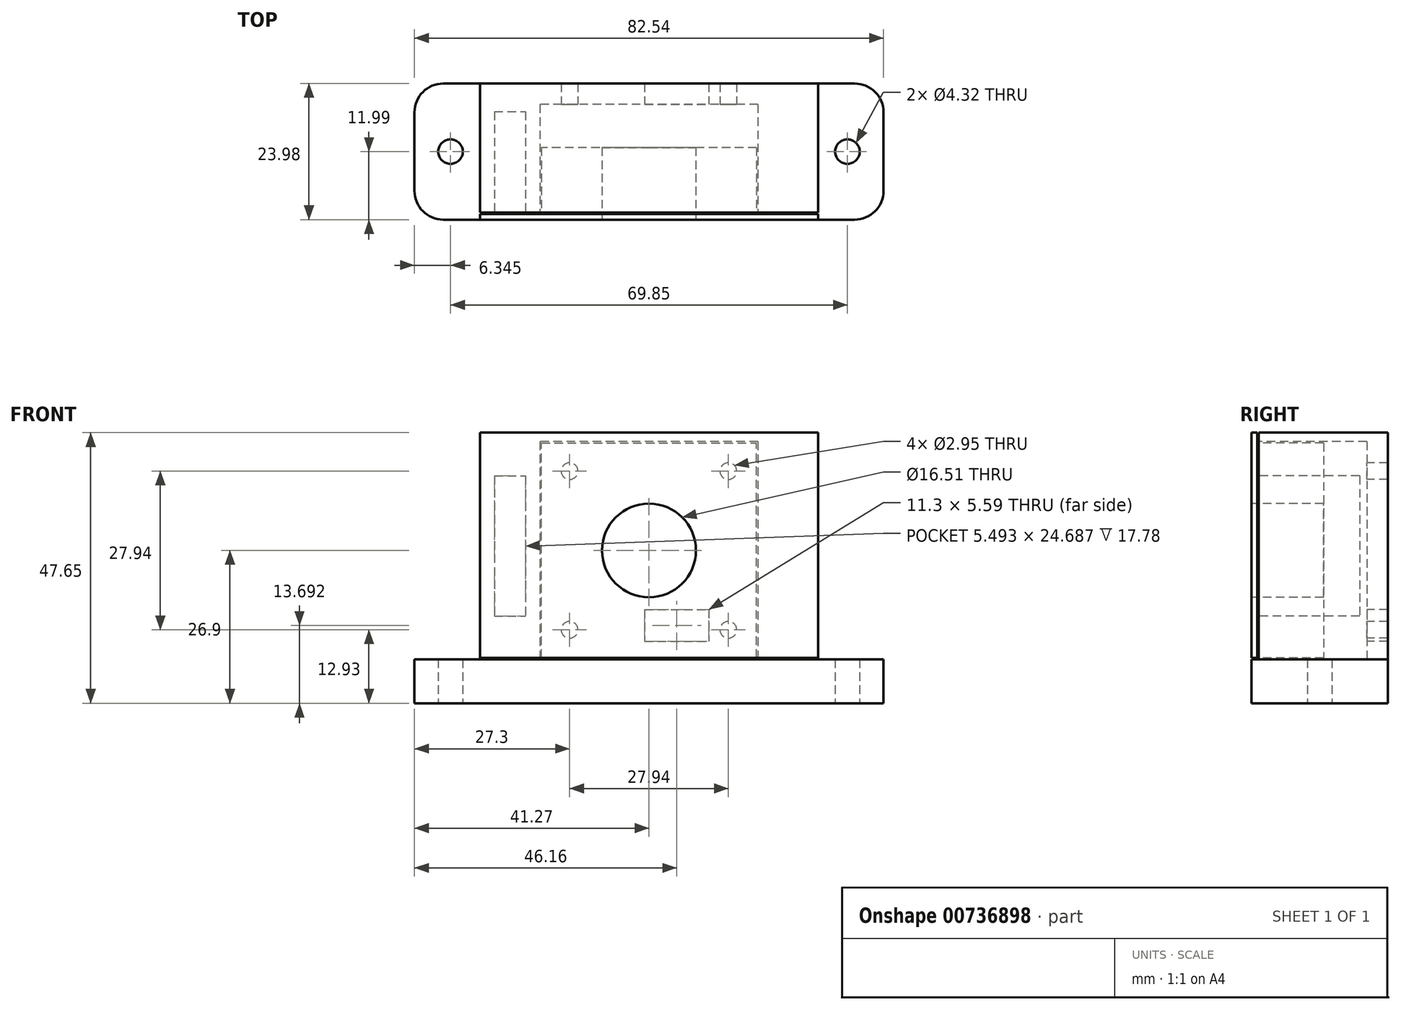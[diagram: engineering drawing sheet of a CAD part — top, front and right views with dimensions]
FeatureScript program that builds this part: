
annotation { "Feature Type Name" : "Feature", "Feature Type Description" : "" }
export const myFeature = defineFeature(function(context is Context, id is Id, definition is map)
    precondition{}
    {
        {
            var Q0;
            Q0=qCreatedBy(makeId("Front.planeOp"),FACE);
            var sketch = newSketch(context, id + "F0", { "sketchPlane" : qUnion([Q0])});
            skLineSegment(sketch, "E0.bottom", {"start": v(-29.75, 20.75) * mm, "end": v(29.75, 20.75) * mm});
            skLineSegment(sketch, "E0.top", {"start": v(-29.75, -20.75) * mm, "end": v(29.75, -20.75) * mm});
            skLineSegment(sketch, "E0.left", {"start": v(-29.75, 20.75) * mm, "end": v(-29.75, -20.75) * mm});
            skLineSegment(sketch, "E0.right", {"start": v(29.75, 20.75) * mm, "end": v(29.75, -20.75) * mm});
            skPoint(sketch, "E0.middle", {"position": v(0, 0) * mm});
            skCircle(sketch, "E1", {"center": v(14.45, 7.05) * mm, "radius": 11.5 * mm});
            skCircle(sketch, "E2", {"center": v(-17.25, -10.75) * mm, "radius": 6 * mm});
            skLineSegment(sketch, "E3.bottom", {"start": v(-22.75, 15.75) * mm, "end": v(-11.25, 15.75) * mm});
            skLineSegment(sketch, "E3.top", {"start": v(-22.75, -1.25) * mm, "end": v(-11.25, -1.25) * mm});
            skLineSegment(sketch, "E3.left", {"start": v(-23.75, 14.75) * mm, "end": v(-23.75, -0.25) * mm});
            skLineSegment(sketch, "E3.right", {"start": v(-10.25, 14.75) * mm, "end": v(-10.25, -0.25) * mm});
            skPoint(sketch, "E4.visualSharp", {"position": v(-10.25, 15.75) * mm});
            skArc(sketch, "E4.filletArc", {"start": v(-10.25, 14.75) * mm, "mid": v(-10.54, 15.46) * mm, "end": v(-11.25, 15.75) * mm});
            skPoint(sketch, "E5.visualSharp", {"position": v(-10.25, -1.25) * mm});
            skArc(sketch, "E5.filletArc", {"start": v(-11.25, -1.25) * mm, "mid": v(-10.54, -0.96) * mm, "end": v(-10.25, -0.25) * mm});
            skPoint(sketch, "E6.visualSharp", {"position": v(-23.75, -1.25) * mm});
            skArc(sketch, "E6.filletArc", {"start": v(-23.75, -0.25) * mm, "mid": v(-23.46, -0.96) * mm, "end": v(-22.75, -1.25) * mm});
            skPoint(sketch, "E7.visualSharp", {"position": v(-23.75, 15.75) * mm});
            skArc(sketch, "E7.filletArc", {"start": v(-22.75, 15.75) * mm, "mid": v(-23.46, 15.46) * mm, "end": v(-23.75, 14.75) * mm});
            skSolve(sketch);
        }
        {
            var Q0;
            Q0=qSketchRegion(id+"F0",true);
            var Q1;
            Q1=makeQuery(id+"F0.imprint","IMPRINT",FACE,{"disambiguationData":[TD([[makeQuery(id+"F0.imprint","IMPRINT",EDGE,{"derivedFrom":sQuery(id+"F0.wireOp",EDGE,"E3.bottom")}),-1.0]])]});
            var Q2;
            Q2=makeQuery(id+"F0.imprint","IMPRINT",FACE,{"disambiguationData":[TD([[makeQuery(id+"F0.imprint","IMPRINT",EDGE,{"derivedFrom":sQuery(id+"F0.wireOp",EDGE,"E1")}),1.0]])]});
            var Q3;
            Q3=makeQuery(id+"F0.imprint","IMPRINT",FACE,{"disambiguationData":[TD([[makeQuery(id+"F0.imprint","IMPRINT",EDGE,{"derivedFrom":sQuery(id+"F0.wireOp",EDGE,"E2")}),1.0]])]});
            extrude(context, id + "F1", {"entities" : qUnion([Q0, Q1, Q2, Q3]), "oppositeDirection" : true, "depth" : 21.5 * mm, "offsetDistance" : 25 * mm});
        }
        {
            var Q0;
            Q0=makeQuery(id+"F1.opExtrude","SWEPT_FACE",FACE,{"disambiguationData":[OSD([sQuery(id+"F0.wireOp",EDGE,"E0.left")])]});
            var sketch = newSketch(context, id + "F2", { "sketchPlane" : qUnion([Q0])});
            skCircle(sketch, "E8", {"center": v(-10, -11.25) * mm, "radius": 2.5 * mm});
            skSolve(sketch);
        }
        {
            var Q0;
            Q0=makeQuery(id+"F1.opExtrude","SWEPT_FACE",FACE,{"disambiguationData":[OSD([sQuery(id+"F0.wireOp",EDGE,"E0.bottom")])]});
            var sketch = newSketch(context, id + "F3", { "sketchPlane" : qUnion([Q0])});
            skCircle(sketch, "E9", {"center": v(-17.25, 10.5) * mm, "radius": 6 * mm});
            skSolve(sketch);
        }
        {
            var Q0;
            Q0=makeQuery(id+"F1.opExtrude","SWEPT_FACE",FACE,{"disambiguationData":[OSD([sQuery(id+"F0.wireOp",EDGE,"E0.right")])]});
            var sketch = newSketch(context, id + "F4", { "sketchPlane" : qUnion([Q0])});
            skLineSegment(sketch, "E10.bottom", {"start": v(5.5, 6.25) * mm, "end": v(15.5, 6.25) * mm});
            skLineSegment(sketch, "E10.top", {"start": v(5.5, -14.25) * mm, "end": v(15.5, -14.25) * mm});
            skLineSegment(sketch, "E10.left", {"start": v(3.5, 4.25) * mm, "end": v(3.5, -12.25) * mm});
            skLineSegment(sketch, "E10.right", {"start": v(17.5, 4.25) * mm, "end": v(17.5, -12.25) * mm});
            skPoint(sketch, "E11.visualSharp", {"position": v(3.5, 6.25) * mm});
            skArc(sketch, "E11.filletArc", {"start": v(5.5, 6.25) * mm, "mid": v(4.09, 5.66) * mm, "end": v(3.5, 4.25) * mm});
            skPoint(sketch, "E12.visualSharp", {"position": v(17.5, 6.25) * mm});
            skArc(sketch, "E12.filletArc", {"start": v(17.5, 4.25) * mm, "mid": v(16.91, 5.66) * mm, "end": v(15.5, 6.25) * mm});
            skPoint(sketch, "E13.visualSharp", {"position": v(17.5, -14.25) * mm});
            skArc(sketch, "E13.filletArc", {"start": v(15.5, -14.25) * mm, "mid": v(16.91, -13.66) * mm, "end": v(17.5, -12.25) * mm});
            skPoint(sketch, "E14.visualSharp", {"position": v(3.5, -14.25) * mm});
            skArc(sketch, "E14.filletArc", {"start": v(3.5, -12.25) * mm, "mid": v(4.09, -13.66) * mm, "end": v(5.5, -14.25) * mm});
            skSolve(sketch);
        }
        {
            var Q0;
            Q0=makeQuery(id+"F0.imprint","IMPRINT",FACE,{"disambiguationData":[TD([[makeQuery(id+"F0.imprint","IMPRINT",EDGE,{"derivedFrom":sQuery(id+"F0.wireOp",EDGE,"E0.bottom")}),-1.0]])]});
            var sketch = newSketch(context, id + "F5", { "sketchPlane" : qUnion([Q0])});
            skLineSegment(sketch, "E15.bottom", {"start": v(-29.75, 20.75) * mm, "end": v(29.75, 20.75) * mm});
            skLineSegment(sketch, "E15.top", {"start": v(-29.75, -20.75) * mm, "end": v(29.75, -20.75) * mm});
            skLineSegment(sketch, "E15.left", {"start": v(-29.75, 20.75) * mm, "end": v(-29.75, -20.75) * mm});
            skLineSegment(sketch, "E15.right", {"start": v(29.75, 20.75) * mm, "end": v(29.75, -20.75) * mm});
            skSolve(sketch);
        }
        {
            var Q0;
            Q0 = qSketchRegion(id + "F5", true);
            extrude(context, id + "F6", {"entities" : qUnion([Q0]), "operationType" : NewBodyOperationType.REMOVE, "endBound" : BoundingType.THROUGH_ALL, "depth" : 25 * mm, "offsetDistance" : 25 * mm});
        }
        {
            var Q0;
            Q0=makeQuery(id+"F6.boolean.opBoolean","MERGE",FACE,{"derivedFrom":[makeQuery(id+"F1.opExtrude","CAP_FACE",FACE,{"disambiguationData":[OSD([sQuery(id+"F0.wireOp",EDGE,"E0.bottom"),sQuery(id+"F0.wireOp",EDGE,"E0.top"),sQuery(id+"F0.wireOp",EDGE,"E0.left"),sQuery(id+"F0.wireOp",EDGE,"E0.right")])],"isStart":true}),makeQuery(id+"F6.opExtrude","CAP_FACE",FACE,{"disambiguationData":[OSD([sQuery(id+"F5.wireOp",EDGE,"E15.bottom"),sQuery(id+"F5.wireOp",EDGE,"E15.top"),sQuery(id+"F5.wireOp",EDGE,"E15.left"),sQuery(id+"F5.wireOp",EDGE,"E15.right")])],"isStart":true})]});
            var sketch = newSketch(context, id + "F7", { "sketchPlane" : qUnion([Q0])});
            skLineSegment(sketch, "E16.bottom", {"start": v(19.18, 19.18) * mm, "end": v(-19.18, 19.18) * mm});
            skLineSegment(sketch, "E16.top", {"start": v(19.18, -19.18) * mm, "end": v(-19.18, -19.18) * mm});
            skLineSegment(sketch, "E16.left", {"start": v(19.18, 19.18) * mm, "end": v(19.18, -19.18) * mm});
            skLineSegment(sketch, "E16.right", {"start": v(-19.18, 19.18) * mm, "end": v(-19.18, -19.18) * mm});
            skPoint(sketch, "E16.middle", {"position": v(0, 0) * mm});
            skSolve(sketch);
        }
        {
            var Q0;
            Q0 = qSketchRegion(id + "F7", true);
            extrude(context, id + "F8", {"entities" : qUnion([Q0]), "operationType" : NewBodyOperationType.REMOVE, "oppositeDirection" : true, "depth" : 19.05 * mm, "offsetDistance" : 25 * mm});
        }
        {
            var Q0;
            Q0=makeQuery(id+"F8.boolean.opBoolean","COPY",FACE,{"derivedFrom":makeQuery(id+"F8.opExtrude","CAP_FACE",FACE,{"disambiguationData":[OSD([sQuery(id+"F7.wireOp",EDGE,"E16.bottom"),sQuery(id+"F7.wireOp",EDGE,"E16.top"),sQuery(id+"F7.wireOp",EDGE,"E16.left"),sQuery(id+"F7.wireOp",EDGE,"E16.right")])],"isStart":false})});
            var sketch = newSketch(context, id + "F9", { "sketchPlane" : qUnion([Q0])});
            skLineSegment(sketch, "E17.bottom", {"start": v(-0.76, -10.41) * mm, "end": v(10.54, -10.41) * mm});
            skLineSegment(sketch, "E17.top", {"start": v(-0.76, -16) * mm, "end": v(10.54, -16) * mm});
            skLineSegment(sketch, "E17.left", {"start": v(-0.76, -10.41) * mm, "end": v(-0.76, -16) * mm});
            skLineSegment(sketch, "E17.right", {"start": v(10.54, -10.41) * mm, "end": v(10.54, -16) * mm});
            skSolve(sketch);
        }
        {
            var Q0;
            Q0=makeQuery(id+"F9.imprint","IMPRINT",FACE,{"disambiguationData":[TD([[makeQuery(id+"F9.imprint","IMPRINT",EDGE,{"derivedFrom":sQuery(id+"F9.wireOp",EDGE,"E17.bottom")}),-1.0]])]});
            extrude(context, id + "F10", {"entities" : qUnion([Q0]), "operationType" : NewBodyOperationType.REMOVE, "endBound" : BoundingType.THROUGH_ALL, "oppositeDirection" : true, "depth" : 25.4 * mm, "offsetDistance" : 25.4 * mm});
        }
        {
            var Q0;
            Q0=makeQuery(id+"F8.boolean.opBoolean","COPY",FACE,{"derivedFrom":makeQuery(id+"F8.opExtrude","CAP_FACE",FACE,{"disambiguationData":[OSD([sQuery(id+"F7.wireOp",EDGE,"E16.bottom"),sQuery(id+"F7.wireOp",EDGE,"E16.top"),sQuery(id+"F7.wireOp",EDGE,"E16.left"),sQuery(id+"F7.wireOp",EDGE,"E16.right")])],"isStart":false})});
            var sketch = newSketch(context, id + "F11", { "sketchPlane" : qUnion([Q0])});
            skLineSegment(sketch, "E18.bottom", {"start": v(13.97, 13.97) * mm, "end": v(-13.97, 13.97) * mm, "construction": true});
            skLineSegment(sketch, "E18.top", {"start": v(13.97, -13.97) * mm, "end": v(-13.97, -13.97) * mm, "construction": true});
            skLineSegment(sketch, "E18.left", {"start": v(13.97, 13.97) * mm, "end": v(13.97, -13.97) * mm, "construction": true});
            skLineSegment(sketch, "E18.right", {"start": v(-13.97, 13.97) * mm, "end": v(-13.97, -13.97) * mm, "construction": true});
            skPoint(sketch, "E18.middle", {"position": v(0, 0) * mm});
            skSolve(sketch);
        }
        {
            var Q0;
            Q0=sQuery(id+"F11.wireOp",VERTEX,"E18.bottom.end");
            var Q1;
            Q1=sQuery(id+"F11.wireOp",VERTEX,"E18.bottom.start");
            var Q2;
            Q2=sQuery(id+"F11.wireOp",VERTEX,"E18.left.end");
            var Q3;
            Q3=sQuery(id+"F11.wireOp",VERTEX,"E18.right.end");
            var Q4;
            Q4=makeQuery(id+"F1.opExtrude","SWEPT_BODY",BODY,{"disambiguationData":[OSD([sQuery(id+"F0.wireOp",EDGE,"E0.bottom"),sQuery(id+"F0.wireOp",EDGE,"E0.top"),sQuery(id+"F0.wireOp",EDGE,"E0.left"),sQuery(id+"F0.wireOp",EDGE,"E0.right")])]});
            hole(context, id + "F12", {"style" : HoleStyle.SIMPLE, "endStyle" : HoleEndStyle.THROUGH, "standardTappedOrClearance" : lookupTablePath({ "standard" : "ANSI", "fit" : "Close", "size" : "#4", "type" : "Clearance" }), "standardBlindInLast" : lookupTablePath({ "fit" : "Close", "standard" : "ANSI", "size" : "#4", "type" : "Clearance" }), "holeDiameter" : 2.95 * mm, "majorDiameter" : 6.35 * mm, "isTappedThrough" : true, "tappedDepth" : 12.7 * mm, "tapClearance" : 3, "locations" : qUnion([Q0, Q1, Q2, Q3]), "scope" : qUnion([Q4])});
        }
        {
            var Q0;
            Q0=makeQuery(id+"F4.imprint","IMPRINT",FACE,{"disambiguationData":[TD([[makeQuery(id+"F4.imprint","IMPRINT",EDGE,{"derivedFrom":sQuery(id+"F4.wireOp",EDGE,"E10.bottom")}),1.0]])]});
            var sketch = newSketch(context, id + "F13", { "sketchPlane" : qUnion([Q0])});
            skLineSegment(sketch, "E19.bottom", {"start": v(0.34, -20.75) * mm, "end": v(21.16, -20.75) * mm});
            skLineSegment(sketch, "E19.top", {"start": v(0.34, -25.32) * mm, "end": v(21.16, -25.32) * mm});
            skLineSegment(sketch, "E19.right", {"start": v(21.16, -20.75) * mm, "end": v(21.16, -25.32) * mm});
            skLineSegment(sketch, "E20", {"start": v(0.34, -20.75) * mm, "end": v(0.34, -25.32) * mm});
            skLineSegment(sketch, "E21.bottom", {"start": v(-1.24, -19.18) * mm, "end": v(22.74, -19.18) * mm});
            skLineSegment(sketch, "E21.top", {"start": v(-1.24, -26.9) * mm, "end": v(22.74, -26.9) * mm});
            skLineSegment(sketch, "E21.left", {"start": v(-1.24, -19.18) * mm, "end": v(-1.24, -26.9) * mm});
            skLineSegment(sketch, "E21.right", {"start": v(22.74, -19.18) * mm, "end": v(22.74, -26.9) * mm});
            skLineSegment(sketch, "E22", {"start": v(10.75, -20.75) * mm, "end": v(10.75, -19.18) * mm, "construction": true});
            skLineSegment(sketch, "E23", {"start": v(22.74, -23.04) * mm, "end": v(21.16, -23.04) * mm, "construction": true});
            skLineSegment(sketch, "E24", {"start": v(10.75, -25.32) * mm, "end": v(10.75, -26.9) * mm, "construction": true});
            skLineSegment(sketch, "E25", {"start": v(0.34, -23.04) * mm, "end": v(-1.24, -23.04) * mm, "construction": true});
            skSolve(sketch);
        }
        {
            var Q0;
            Q0 = qSketchRegion(id + "F13", true);
            var Q1;
            Q1=makeQuery(id+"F1.opExtrude","SWEPT_FACE",FACE,{"disambiguationData":[OSD([sQuery(id+"F0.wireOp",EDGE,"E0.left")])]});
            extrude(context, id + "F14", {"entities" : qUnion([Q0]), "operationType" : NewBodyOperationType.ADD, "endBound" : BoundingType.UP_TO_SURFACE, "oppositeDirection" : true, "depth" : 25.4 * mm, "endBoundEntityFace" : qUnion([Q1]), "offsetDistance" : 25.4 * mm});
        }
        {
            var Q0;
            Q0=makeQuery(id+"F1.opExtrude","CAP_FACE",FACE,{"disambiguationData":[OSD([sQuery(id+"F0.wireOp",EDGE,"E0.bottom"),sQuery(id+"F0.wireOp",EDGE,"E0.top"),sQuery(id+"F0.wireOp",EDGE,"E0.left"),sQuery(id+"F0.wireOp",EDGE,"E0.right")])],"isStart":false});
            var Q1;
            Q1=makeQuery(id+"F14.opExtrude","SWEPT_FACE",FACE,{"disambiguationData":[OSD([sQuery(id+"F13.wireOp",EDGE,"E21.right")])]});
            extrude(context, id + "F15", {"entities" : qUnion([Q0]), "operationType" : NewBodyOperationType.ADD, "endBound" : BoundingType.UP_TO_SURFACE, "depth" : 25.4 * mm, "endBoundEntityFace" : qUnion([Q1]), "offsetDistance" : 25.4 * mm});
        }
        {
            var Q0;
            Q0=makeQuery(id+"F1.opExtrude","CAP_FACE",FACE,{"disambiguationData":[OSD([sQuery(id+"F0.wireOp",EDGE,"E0.bottom"),sQuery(id+"F0.wireOp",EDGE,"E0.top"),sQuery(id+"F0.wireOp",EDGE,"E0.left"),sQuery(id+"F0.wireOp",EDGE,"E0.right")])],"isStart":true});
            var sketch = newSketch(context, id + "F16", { "sketchPlane" : qUnion([Q0])});
            skLineSegment(sketch, "E26.bottom", {"start": v(-27.21, 13.13) * mm, "end": v(-21.72, 13.13) * mm});
            skLineSegment(sketch, "E26.top", {"start": v(-27.21, -11.56) * mm, "end": v(-21.72, -11.56) * mm});
            skLineSegment(sketch, "E26.left", {"start": v(-27.2, 13.13) * mm, "end": v(-27.21, -11.56) * mm});
            skLineSegment(sketch, "E26.right", {"start": v(-21.72, 13.13) * mm, "end": v(-21.72, -11.56) * mm});
            skSolve(sketch);
        }
        {
            var Q0;
            Q0 = qSketchRegion(id + "F16", true);
            extrude(context, id + "F17", {"entities" : qUnion([Q0]), "operationType" : NewBodyOperationType.REMOVE, "oppositeDirection" : true, "depth" : 17.78 * mm, "offsetDistance" : 25.4 * mm});
        }
        {
            var Q0;
            Q0=makeQuery(id+"F14.opExtrude","SWEPT_FACE",FACE,{"disambiguationData":[OSD([sQuery(id+"F13.wireOp",EDGE,"E21.left")])]});
            var sketch = newSketch(context, id + "F18", { "sketchPlane" : qUnion([Q0])});
            skLineSegment(sketch, "E27.2", {"start": v(-18.92, -18.92) * mm, "end": v(18.92, -18.92) * mm});
            skCircle(sketch, "E28", {"center": v(0, 0) * mm, "radius": 8.26 * mm});
            skLineSegment(sketch, "E29.0", {"start": v(-18.92, 18.92) * mm, "end": v(-18.92, -18.92) * mm});
            skLineSegment(sketch, "E29.1", {"start": v(18.92, 18.92) * mm, "end": v(-18.92, 18.92) * mm});
            skLineSegment(sketch, "E29.2", {"start": v(18.92, 18.92) * mm, "end": v(18.92, -18.92) * mm});
            skSolve(sketch);
        }
        {
            var Q0;
            Q0 = qSketchRegion(id + "F18", true);
            extrude(context, id + "F19", {"entities" : qUnion([Q0]), "oppositeDirection" : true, "depth" : 12.7 * mm, "offsetDistance" : 25.4 * mm});
        }
        {
            var Q0;
            Q0=makeQuery(id+"F19.opExtrude","CAP_FACE",FACE,{"disambiguationData":[OSD([sQuery(id+"F18.wireOp",EDGE,"E27.2"),sQuery(id+"F18.wireOp",EDGE,"E28"),sQuery(id+"F18.wireOp",EDGE,"E29.0"),sQuery(id+"F18.wireOp",EDGE,"E29.1"),sQuery(id+"F18.wireOp",EDGE,"E29.2")])],"isStart":true});
            var sketch = newSketch(context, id + "F20", { "sketchPlane" : qUnion([Q0])});
            skLineSegment(sketch, "E30.bottom", {"start": v(-29.75, 20.75) * mm, "end": v(29.75, 20.75) * mm});
            skLineSegment(sketch, "E30.top", {"start": v(-29.75, -18.92) * mm, "end": v(29.75, -18.92) * mm});
            skLineSegment(sketch, "E30.left", {"start": v(-29.75, 20.75) * mm, "end": v(-29.75, -18.92) * mm});
            skLineSegment(sketch, "E30.right", {"start": v(29.75, 20.75) * mm, "end": v(29.75, -18.92) * mm});
            skCircle(sketch, "E31.0", {"center": v(0, 0) * mm, "radius": 8.26 * mm});
            skSolve(sketch);
        }
        {
            var Q0;
            Q0 = qSketchRegion(id + "F20", true);
            extrude(context, id + "F21", {"entities" : qUnion([Q0]), "operationType" : NewBodyOperationType.ADD, "oppositeDirection" : true, "depth" : 1.02 * mm, "offsetDistance" : 25.4 * mm});
        }
        {
            var Q0;
            Q0=qCreatedBy(makeId("Right.planeOp"),FACE);
            var sketch = newSketch(context, id + "F22", { "sketchPlane" : qUnion([Q0])});
            skLineSegment(sketch, "E32.bottom", {"start": v(22.74, -19.18) * mm, "end": v(-1.24, -19.18) * mm});
            skLineSegment(sketch, "E32.top", {"start": v(22.74, -26.9) * mm, "end": v(-1.24, -26.9) * mm});
            skLineSegment(sketch, "E32.left", {"start": v(22.74, -19.18) * mm, "end": v(22.74, -26.9) * mm});
            skLineSegment(sketch, "E32.right", {"start": v(-1.24, -19.18) * mm, "end": v(-1.24, -26.9) * mm});
            skSolve(sketch);
        }
        {
            var Q0;
            Q0 = qSketchRegion(id + "F22", true);
            extrude(context, id + "F23", {"entities" : qUnion([Q0]), "operationType" : NewBodyOperationType.ADD, "endBound" : BoundingType.SYMMETRIC, "depth" : 82.55 * mm, "offsetDistance" : 25.4 * mm});
        }
        {
            var Q0;
            Q0=makeQuery(id+"F23.boolean.opBoolean","MERGE",FACE,{"derivedFrom":[makeQuery(id+"F14.opExtrude","SWEPT_FACE",FACE,{"disambiguationData":[OSD([sQuery(id+"F13.wireOp",EDGE,"E21.top")])]}),makeQuery(id+"F23.opExtrude","SWEPT_FACE",FACE,{"disambiguationData":[OSD([sQuery(id+"F22.wireOp",EDGE,"E32.top")])]})]});
            var sketch = newSketch(context, id + "F24", { "sketchPlane" : qUnion([Q0])});
            skCircle(sketch, "E33", {"center": v(-34.92, -10.75) * mm, "radius": 2.16 * mm});
            skCircle(sketch, "E34", {"center": v(34.93, -10.75) * mm, "radius": 2.16 * mm});
            skLineSegment(sketch, "E35", {"start": v(-41.27, -10.75) * mm, "end": v(41.28, -10.75) * mm, "construction": true});
            skLineSegment(sketch, "E36", {"start": v(-34.92, -10.75) * mm, "end": v(0, 1.24) * mm, "construction": true});
            skLineSegment(sketch, "E37", {"start": v(0, 1.24) * mm, "end": v(34.93, -10.75) * mm, "construction": true});
            skSolve(sketch);
        }
        {
            var Q0;
            Q0 = qSketchRegion(id + "F24", true);
            extrude(context, id + "F25", {"entities" : qUnion([Q0]), "operationType" : NewBodyOperationType.REMOVE, "oppositeDirection" : true, "depth" : 25.4 * mm, "offsetDistance" : 25.4 * mm});
        }
        {
            var Q0;
            Q0=makeQuery(id+"F23.opExtrude","CAP_EDGE",EDGE,{"disambiguationData":[OSD([sQuery(id+"F22.wireOp",EDGE,"E32.left")])],"isStart":true});
            var Q1;
            Q1=makeQuery(id+"F23.opExtrude","CAP_EDGE",EDGE,{"disambiguationData":[OSD([sQuery(id+"F22.wireOp",EDGE,"E32.right")])],"isStart":true});
            var Q2;
            Q2=makeQuery(id+"F23.opExtrude","CAP_EDGE",EDGE,{"disambiguationData":[OSD([sQuery(id+"F22.wireOp",EDGE,"E32.left")])],"isStart":false});
            var Q3;
            Q3=makeQuery(id+"F23.opExtrude","CAP_EDGE",EDGE,{"disambiguationData":[OSD([sQuery(id+"F22.wireOp",EDGE,"E32.right")])],"isStart":false});
            fillet(context, id + "F26", {"entities" : qUnion([Q0, Q1, Q2, Q3]), "radius" : 5.08 * mm, "tangentPropagation" : true, "allowEdgeOverflow" : false});
        }
    });
